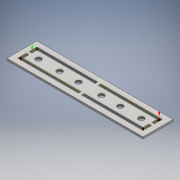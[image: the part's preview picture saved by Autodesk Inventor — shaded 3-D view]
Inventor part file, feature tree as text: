
AUTODESK INVENTOR PART (.ipt)
format: ipt  version: 2016 (Build 200138000, 138)  size: 656,896 bytes
history: native  units: mm
features: extrude x1, sketch x1
ambient origin geometry x8: Origin, YZ Plane, XZ Plane, XY Plane, X Axis, Y Axis, Z Axis, Center Point
bodies: Body1 (feature_tree)
feature tree (2):
  extrude  "Extrusion4"  Depth=9.525mm
  sketch  "Sketch1"  dims[d4=26.0mm d6=26.0mm d8=26.0mm d10=26.0mm d12=26.0mm d14=26.0mm d16=568.96mm d18=40.64mm d19=140.776mm d20=230.152mm d21=230.152mm d22=40.64mm d23=140.776mm d29=66.305mm d45=33.1525mm d46=33.1525mm d47=33.1525mm d48=33.1525mm d49=33.1525mm d50=33.1525mm d52=12.7mm d53=12.7mm d54=25.4mm d56=25.4mm d57=15.0mm d58=9.525mm d59=0.0mm]
